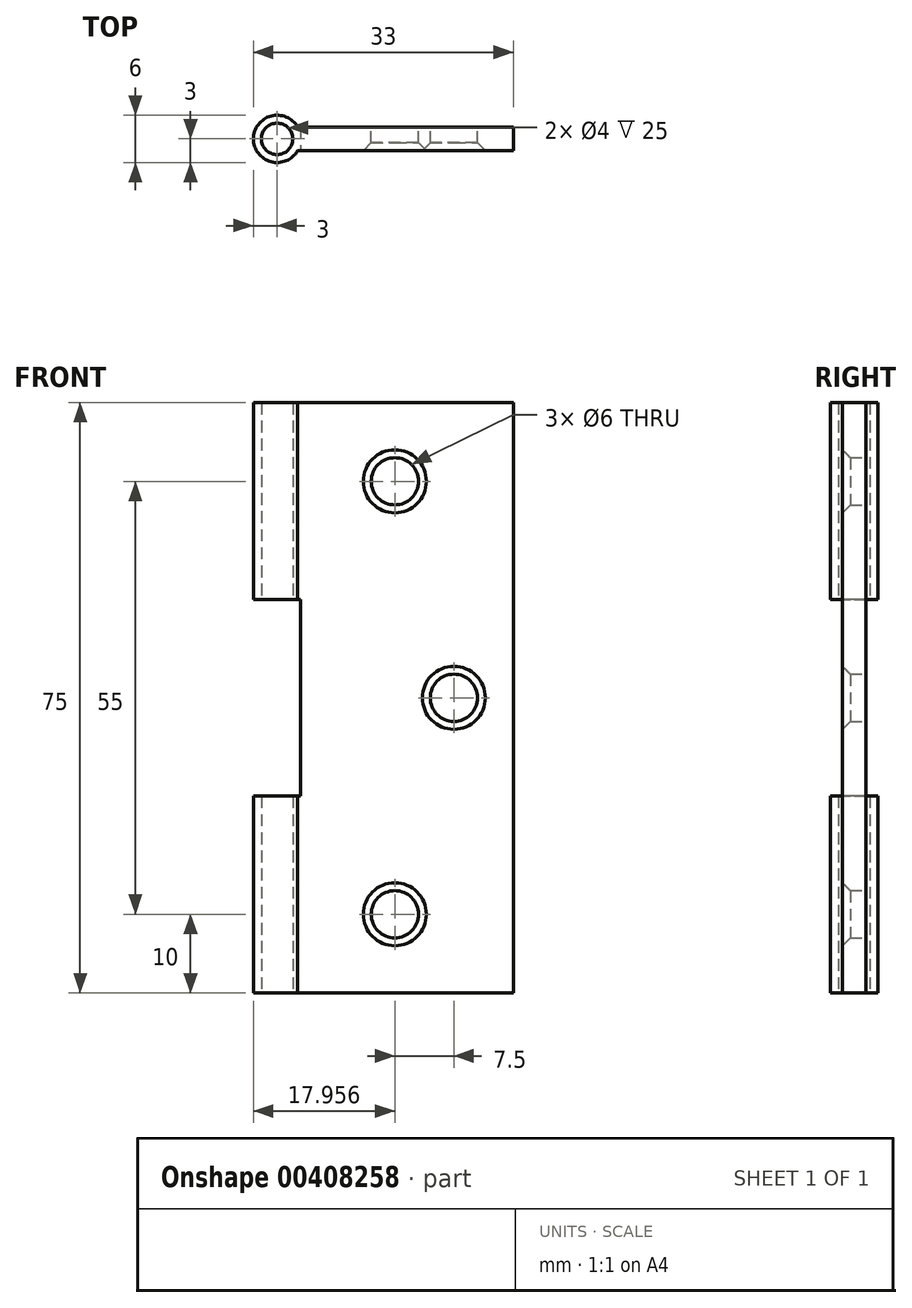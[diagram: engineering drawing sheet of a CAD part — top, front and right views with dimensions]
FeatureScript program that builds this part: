
annotation { "Feature Type Name" : "Feature", "Feature Type Description" : "" }
export const myFeature = defineFeature(function(context is Context, id is Id, definition is map)
    precondition{}
    {
        {
            var Q0;
            Q0=qCreatedBy(makeId("Top.planeOp"),FACE);
            var sketch = newSketch(context, id + "F0", { "sketchPlane" : qUnion([Q0])});
            skLineSegment(sketch, "E0", {"start": v(30, 1.5) * mm, "end": v(30, -1.5) * mm});
            skPoint(sketch, "E1.orphan", {"position": v(0, 2) * mm});
            skPoint(sketch, "E2.orphan", {"position": v(0, -2) * mm});
            skCircle(sketch, "E3", {"center": v(0, 0) * mm, "radius": 2 * mm});
            skArc(sketch, "E4", {"start": v(2.6, 1.5) * mm, "mid": v(-3, 0) * mm, "end": v(2.6, -1.5) * mm});
            skLineSegment(sketch, "E5.trimOffspring", {"start": v(2.6, 1.5) * mm, "end": v(30, 1.5) * mm});
            skLineSegment(sketch, "E6.trimOffspring", {"start": v(2.6, -1.5) * mm, "end": v(30, -1.5) * mm});
            skPoint(sketch, "E7.trimOffspring.end.orphan", {"position": v(30, 0) * mm});
            skPoint(sketch, "E8.orphan", {"position": v(30, 2) * mm});
            skPoint(sketch, "E9.orphan", {"position": v(30, -2) * mm});
            skSolve(sketch);
        }
        {
            var Q0;
            Q0 = qSketchRegion(id + "F0", true);
            extrude(context, id + "F1", {"entities" : qUnion([Q0]), "depth" : 75 * mm});
        }
        {
            var Q0;
            Q0=qCreatedBy(makeId("Front.planeOp"),FACE);
            var sketch = newSketch(context, id + "F2", { "sketchPlane" : qUnion([Q0])});
            skLineSegment(sketch, "E10", {"start": v(0, 0) * mm, "end": v(0, 75) * mm});
            skLineSegment(sketch, "E11.bottom", {"start": v(3, 50) * mm, "end": v(-3, 50) * mm});
            skLineSegment(sketch, "E11.top", {"start": v(3, 25) * mm, "end": v(-3, 25) * mm});
            skLineSegment(sketch, "E11.left", {"start": v(3, 50) * mm, "end": v(3, 25) * mm});
            skLineSegment(sketch, "E11.right", {"start": v(-3, 50) * mm, "end": v(-3, 25) * mm});
            skPoint(sketch, "E11.middle", {"position": v(0, 37.5) * mm});
            skSolve(sketch);
        }
        {
            var Q0;
            Q0 = qSketchRegion(id + "F2", true);
            extrude(context, id + "F3", {"entities" : qUnion([Q0]), "operationType" : NewBodyOperationType.REMOVE, "oppositeDirection" : true, "depth" : 25 * mm, "symmetric" : true});
        }
        {
            var Q0;
            Q0=makeQuery(id+"F1.opExtrude","SWEPT_FACE",FACE,{"disambiguationData":[OSD([sQuery(id+"F0.wireOp",EDGE,"E6.trimOffspring")])]});
            var sketch = newSketch(context, id + "F4", { "sketchPlane" : qUnion([Q0])});
            skLineSegment(sketch, "E12", {"start": v(0, 0) * mm, "end": v(30, 0) * mm});
            skPoint(sketch, "E13", {"position": v(14.96, 65) * mm});
            skPoint(sketch, "E14", {"position": v(14.96, 10) * mm});
            skPoint(sketch, "E15", {"position": v(22.46, 37.5) * mm});
            skSolve(sketch);
        }
        {
            var Q0;
            Q0=sQuery(id+"F4.wireOp",VERTEX,"E13");
            var Q1;
            Q1=sQuery(id+"F4.wireOp",VERTEX,"E15");
            var Q2;
            Q2=sQuery(id+"F4.wireOp",VERTEX,"E14");
            var Q3;
            Q3=makeQuery(id+"F1.opExtrude","SWEPT_BODY",BODY,{"disambiguationData":[OSD([sQuery(id+"F0.wireOp",EDGE,"E0"),sQuery(id+"F0.wireOp",EDGE,"E3"),sQuery(id+"F0.wireOp",EDGE,"E4"),sQuery(id+"F0.wireOp",EDGE,"E5.trimOffspring"),sQuery(id+"F0.wireOp",EDGE,"E6.trimOffspring")])]});
            hole(context, id + "F5", {"style" : HoleStyle.C_SINK, "endStyle" : HoleEndStyle.THROUGH, "holeDiameter" : 6 * mm, "cSinkDiameter" : 8 * mm, "cSinkAngle" : 90 * degree, "isTappedThrough" : true, "tappedDepth" : 12 * mm, "tapClearance" : 3, "locations" : qUnion([Q0, Q1, Q2]), "scope" : qUnion([Q3])});
        }
    });
